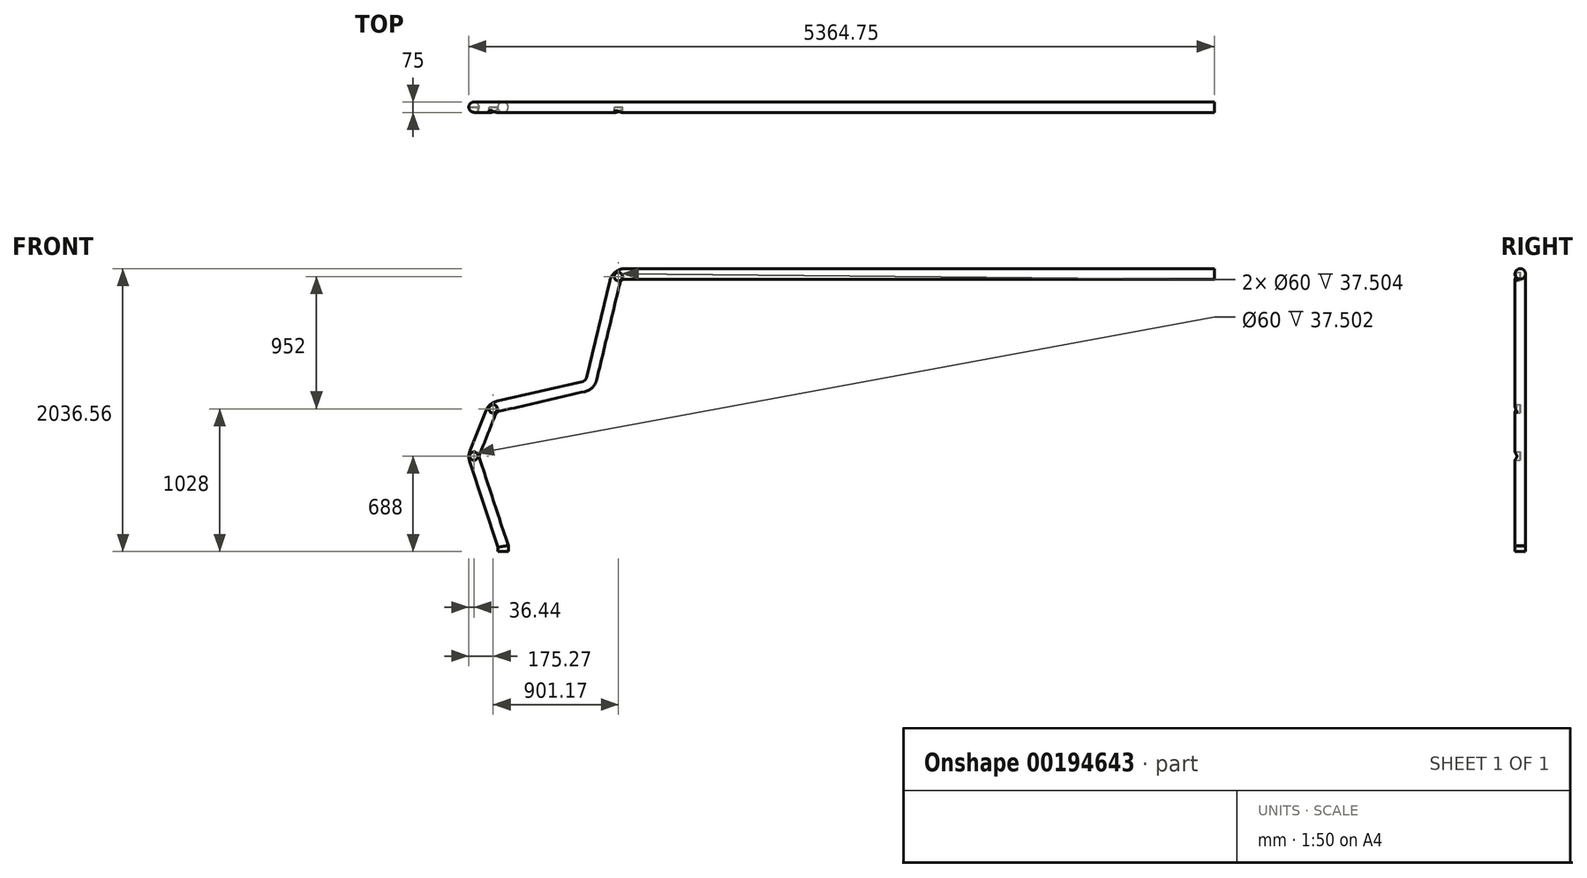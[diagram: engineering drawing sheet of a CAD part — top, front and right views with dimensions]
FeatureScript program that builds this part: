
annotation { "Feature Type Name" : "Feature", "Feature Type Description" : "" }
export const myFeature = defineFeature(function(context is Context, id is Id, definition is map)
    precondition{}
    {
        {
            var Q0;
            Q0=qCreatedBy(makeId("Top.planeOp"),FACE);
            var sketch = newSketch(context, id + "F0", { "sketchPlane" : qUnion([Q0])});
            skCircle(sketch, "E0", {"center": v(0, 0) * mm, "radius": 37.5 * mm});
            skSolve(sketch);
        }
        {
            var Q0;
            Q0=qCreatedBy(makeId("Front.planeOp"),FACE);
            var sketch = newSketch(context, id + "F1", { "sketchPlane" : qUnion([Q0])});
            skLineSegment(sketch, "E1", {"start": v(0, 0) * mm, "end": v(0, 37.5) * mm});
            skLineSegment(sketch, "E2", {"start": v(0, 37.5) * mm, "end": v(-205.18, 661.57) * mm});
            skLineSegment(sketch, "E3", {"start": v(-203.57, 712.85) * mm, "end": v(-88.28, 1001.1) * mm});
            skLineSegment(sketch, "E4", {"start": v(-35.51, 1046.32) * mm, "end": v(581.05, 1188.62) * mm});
            skLineSegment(sketch, "E5", {"start": v(637.12, 1244.2) * mm, "end": v(804.51, 1941.56) * mm});
            skPoint(sketch, "E6.visualSharp", {"position": v(-213.7, 687.5) * mm});
            skArc(sketch, "E6.filletArc", {"start": v(-203.57, 712.85) * mm, "mid": v(-208.9, 687.35) * mm, "end": v(-205.18, 661.57) * mm});
            skPoint(sketch, "E7.visualSharp", {"position": v(-73.72, 1037.5) * mm});
            skArc(sketch, "E7.filletArc", {"start": v(-35.51, 1046.32) * mm, "mid": v(-67.45, 1030.19) * mm, "end": v(-88.28, 1001.1) * mm});
            skPoint(sketch, "E8.visualSharp", {"position": v(626.28, 1199.06) * mm});
            skArc(sketch, "E8.filletArc", {"start": v(581.05, 1188.62) * mm, "mid": v(616.99, 1208.43) * mm, "end": v(637.12, 1244.2) * mm});
            skLineSegment(sketch, "E9", {"start": v(877.44, 1999.06) * mm, "end": v(5118.31, 1999.06) * mm});
            skPoint(sketch, "E10.visualSharp", {"position": v(818.31, 1999.06) * mm});
            skArc(sketch, "E10.filletArc", {"start": v(877.44, 1999.06) * mm, "mid": v(831, 1982.95) * mm, "end": v(804.51, 1941.56) * mm});
            skSolve(sketch);
        }
        {
            var Q0;
            Q0=makeQuery(id+"F0.imprint","IMPRINT",FACE,{"disambiguationData":[TD([[makeQuery(id+"F0.imprint","IMPRINT",EDGE,{"derivedFrom":sQuery(id+"F0.wireOp",EDGE,"E0")}),1.0]])]});
            var Q1;
            Q1=sQuery(id+"F1.wireOp",EDGE,"E1");
            var Q2;
            Q2=sQuery(id+"F1.wireOp",EDGE,"E2");
            var Q3;
            Q3=sQuery(id+"F1.wireOp",EDGE,"E6.filletArc");
            var Q4;
            Q4=sQuery(id+"F1.wireOp",EDGE,"E3");
            var Q5;
            Q5=sQuery(id+"F1.wireOp",EDGE,"E7.filletArc");
            var Q6;
            Q6=sQuery(id+"F1.wireOp",EDGE,"E4");
            var Q7;
            Q7=sQuery(id+"F1.wireOp",EDGE,"E8.filletArc");
            var Q8;
            Q8=sQuery(id+"F1.wireOp",EDGE,"E5");
            var Q9;
            Q9=sQuery(id+"F1.wireOp",EDGE,"E10.filletArc");
            var Q10;
            Q10=sQuery(id+"F1.wireOp",EDGE,"E9");
            sweep(context, id + "F2", {"profiles" : qUnion([Q0]), "path" : qUnion([Q1, Q2, Q3, Q4, Q5, Q6, Q7, Q8, Q9, Q10])});
        }
        {
            var Q0;
            Q0=qCreatedBy(makeId("Front.planeOp"),FACE);
            var sketch = newSketch(context, id + "F3", { "sketchPlane" : qUnion([Q0])});
            skCircle(sketch, "E11", {"center": v(-210, 688) * mm, "radius": 30 * mm});
            skCircle(sketch, "E12", {"center": v(-71.17, 1028) * mm, "radius": 30 * mm});
            skCircle(sketch, "E13", {"center": v(830, 1980) * mm, "radius": 30 * mm});
            skSolve(sketch);
        }
        {
            var Q0;
            Q0 = qSketchRegion(id + "F3", true);
            extrude(context, id + "F4", {"entities" : qUnion([Q0]), "operationType" : NewBodyOperationType.REMOVE, "depth" : 37.5 * mm});
        }
    });
